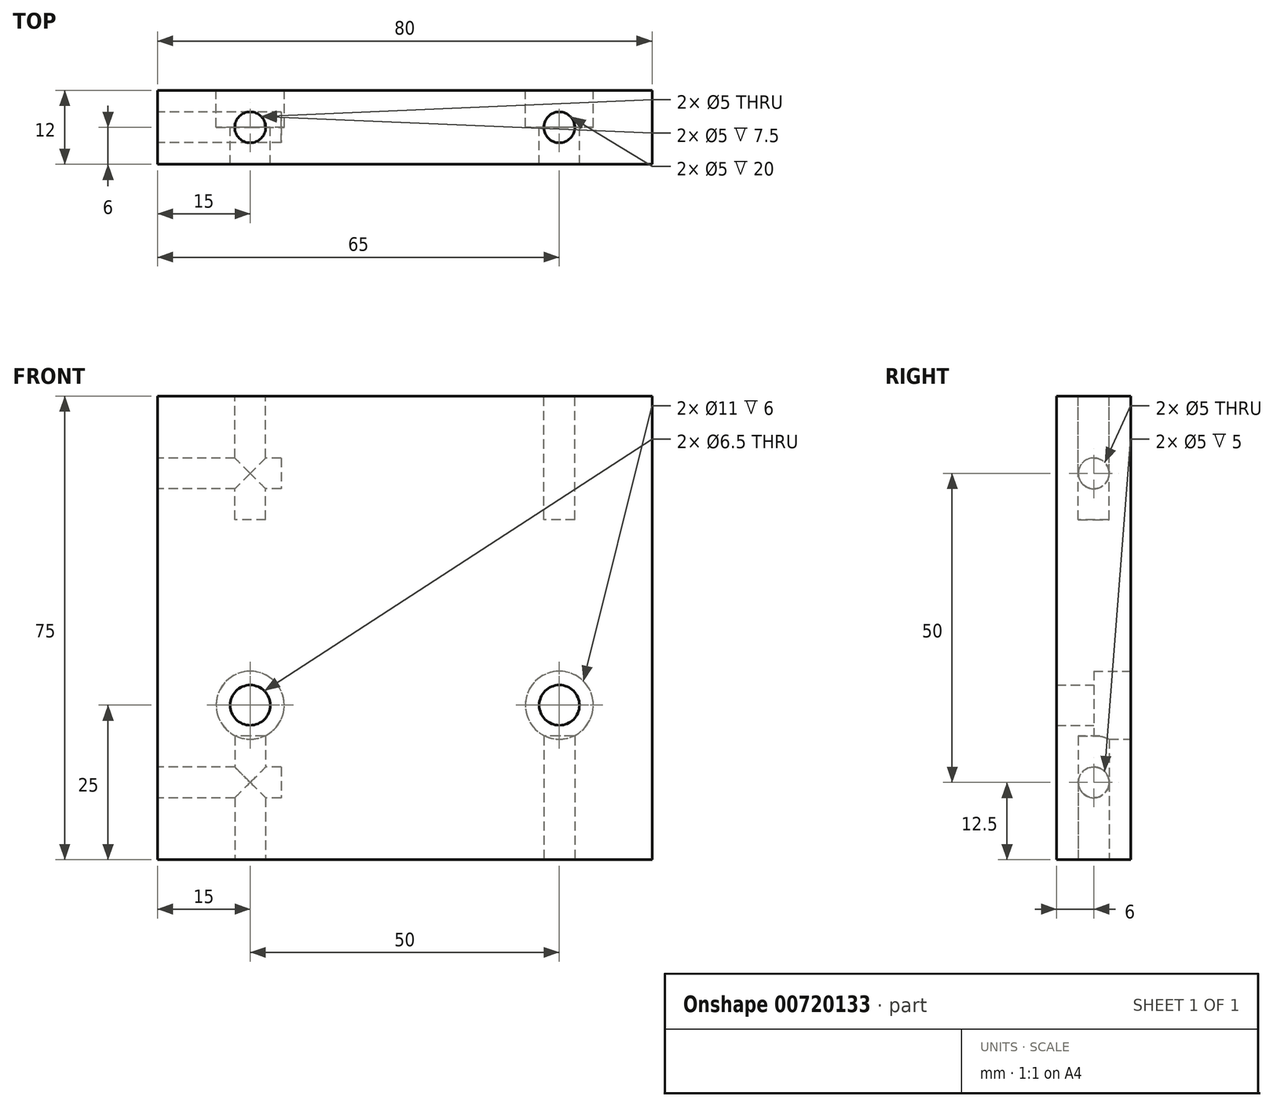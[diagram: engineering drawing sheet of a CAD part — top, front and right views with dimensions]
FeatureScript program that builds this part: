
annotation { "Feature Type Name" : "Feature", "Feature Type Description" : "" }
export const myFeature = defineFeature(function(context is Context, id is Id, definition is map)
    precondition{}
    {
        {
            var Q0;
            Q0=qCreatedBy(makeId("Front.planeOp"),FACE);
            var sketch = newSketch(context, id + "F0", { "sketchPlane" : qUnion([Q0])});
            skLineSegment(sketch, "E0.bottom", {"start": v(0, 0) * mm, "end": v(80, 0) * mm});
            skLineSegment(sketch, "E0.top", {"start": v(0, 75) * mm, "end": v(80, 75) * mm});
            skLineSegment(sketch, "E0.left", {"start": v(0, 0) * mm, "end": v(0, 75) * mm});
            skLineSegment(sketch, "E0.right", {"start": v(80, 0) * mm, "end": v(80, 75) * mm});
            skCircle(sketch, "E1", {"center": v(15, 25) * mm, "radius": 3.25 * mm});
            skCircle(sketch, "E2", {"center": v(65, 25) * mm, "radius": 3.25 * mm});
            skSolve(sketch);
        }
        {
            var Q0;
            Q0=makeQuery(id+"F0.imprint","IMPRINT",FACE,{"disambiguationData":[TD([[makeQuery(id+"F0.imprint","IMPRINT",EDGE,{"derivedFrom":sQuery(id+"F0.wireOp",EDGE,"E0.bottom")}),1.0]])]});
            extrude(context, id + "F1", {"entities" : qUnion([Q0]), "depth" : 12 * mm, "offsetDistance" : 25 * mm});
        }
        {
            var Q0;
            Q0=makeQuery(id+"F1.opExtrude","CAP_FACE",FACE,{"disambiguationData":[OSD([sQuery(id+"F0.wireOp",EDGE,"E0.bottom"),sQuery(id+"F0.wireOp",EDGE,"E0.top"),sQuery(id+"F0.wireOp",EDGE,"E0.left"),sQuery(id+"F0.wireOp",EDGE,"E0.right"),sQuery(id+"F0.wireOp",EDGE,"E1"),sQuery(id+"F0.wireOp",EDGE,"E2")])],"isStart":true});
            var sketch = newSketch(context, id + "F2", { "sketchPlane" : qUnion([Q0])});
            skCircle(sketch, "E3", {"center": v(-15, 25) * mm, "radius": 5.5 * mm});
            skCircle(sketch, "E4", {"center": v(-65, 25) * mm, "radius": 5.5 * mm});
            skSolve(sketch);
        }
        {
            var Q0;
            Q0=qSketchRegion(id+"F2",true);
            extrude(context, id + "F3", {"entities" : qUnion([Q0]), "operationType" : NewBodyOperationType.REMOVE, "oppositeDirection" : true, "depth" : 6 * mm, "offsetDistance" : 25 * mm});
        }
        {
            var Q0;
            Q0=makeQuery(id+"F1.opExtrude","SWEPT_FACE",FACE,{"disambiguationData":[OSD([sQuery(id+"F0.wireOp",EDGE,"E0.bottom")])]});
            var sketch = newSketch(context, id + "F4", { "sketchPlane" : qUnion([Q0])});
            skCircle(sketch, "E5", {"center": v(15, 6) * mm, "radius": 2.5 * mm});
            skPoint(sketch, "E5.centerSnap0", {"position": v(0, 6) * mm});
            skCircle(sketch, "E6", {"center": v(65, 6) * mm, "radius": 2.5 * mm});
            skSolve(sketch);
        }
        {
            var Q0;
            Q0=makeQuery(id+"F4.imprint","IMPRINT",FACE,{"disambiguationData":[TD([[makeQuery(id+"F4.imprint","IMPRINT",EDGE,{"derivedFrom":sQuery(id+"F4.wireOp",EDGE,"E5")}),1.0]])]});
            var Q1;
            Q1=makeQuery(id+"F4.imprint","IMPRINT",FACE,{"disambiguationData":[TD([[makeQuery(id+"F4.imprint","IMPRINT",EDGE,{"derivedFrom":sQuery(id+"F4.wireOp",EDGE,"E6")}),1.0]])]});
            extrude(context, id + "F5", {"entities" : qUnion([Q0, Q1]), "operationType" : NewBodyOperationType.REMOVE, "oppositeDirection" : true, "depth" : 20 * mm, "offsetDistance" : 25 * mm});
        }
        {
            var Q0;
            Q0=makeQuery(id+"F1.opExtrude","SWEPT_FACE",FACE,{"disambiguationData":[OSD([sQuery(id+"F0.wireOp",EDGE,"E0.top")])]});
            var sketch = newSketch(context, id + "F6", { "sketchPlane" : qUnion([Q0])});
            skCircle(sketch, "E7", {"center": v(15, -6) * mm, "radius": 2.5 * mm});
            skCircle(sketch, "E8", {"center": v(65, -6) * mm, "radius": 2.5 * mm});
            skSolve(sketch);
        }
        {
            var Q0;
            Q0=makeQuery(id+"F6.imprint","IMPRINT",FACE,{"disambiguationData":[TD([[makeQuery(id+"F6.imprint","IMPRINT",EDGE,{"derivedFrom":sQuery(id+"F6.wireOp",EDGE,"E7")}),1.0]])]});
            var Q1;
            Q1=makeQuery(id+"F6.imprint","IMPRINT",FACE,{"disambiguationData":[TD([[makeQuery(id+"F6.imprint","IMPRINT",EDGE,{"derivedFrom":sQuery(id+"F6.wireOp",EDGE,"E8")}),1.0]])]});
            extrude(context, id + "F7", {"entities" : qUnion([Q0, Q1]), "operationType" : NewBodyOperationType.REMOVE, "oppositeDirection" : true, "depth" : 20 * mm, "offsetDistance" : 25 * mm});
        }
        {
            var Q0;
            Q0=makeQuery(id+"F1.opExtrude","SWEPT_FACE",FACE,{"disambiguationData":[OSD([sQuery(id+"F0.wireOp",EDGE,"E0.left")])]});
            var sketch = newSketch(context, id + "F8", { "sketchPlane" : qUnion([Q0])});
            skCircle(sketch, "E9", {"center": v(6, 62.5) * mm, "radius": 2.5 * mm});
            skPoint(sketch, "E9.centerSnap0", {"position": v(6, 75) * mm});
            skCircle(sketch, "E10", {"center": v(6, 12.5) * mm, "radius": 2.5 * mm});
            skSolve(sketch);
        }
        {
            var Q0;
            Q0=makeQuery(id+"F8.imprint","IMPRINT",FACE,{"disambiguationData":[TD([[makeQuery(id+"F8.imprint","IMPRINT",EDGE,{"derivedFrom":sQuery(id+"F8.wireOp",EDGE,"E9")}),1.0]])]});
            var Q1;
            Q1=makeQuery(id+"F8.imprint","IMPRINT",FACE,{"disambiguationData":[TD([[makeQuery(id+"F8.imprint","IMPRINT",EDGE,{"derivedFrom":sQuery(id+"F8.wireOp",EDGE,"E10")}),1.0]])]});
            extrude(context, id + "F9", {"entities" : qUnion([Q0, Q1]), "operationType" : NewBodyOperationType.REMOVE, "oppositeDirection" : true, "depth" : 20 * mm, "offsetDistance" : 25 * mm});
        }
    });
